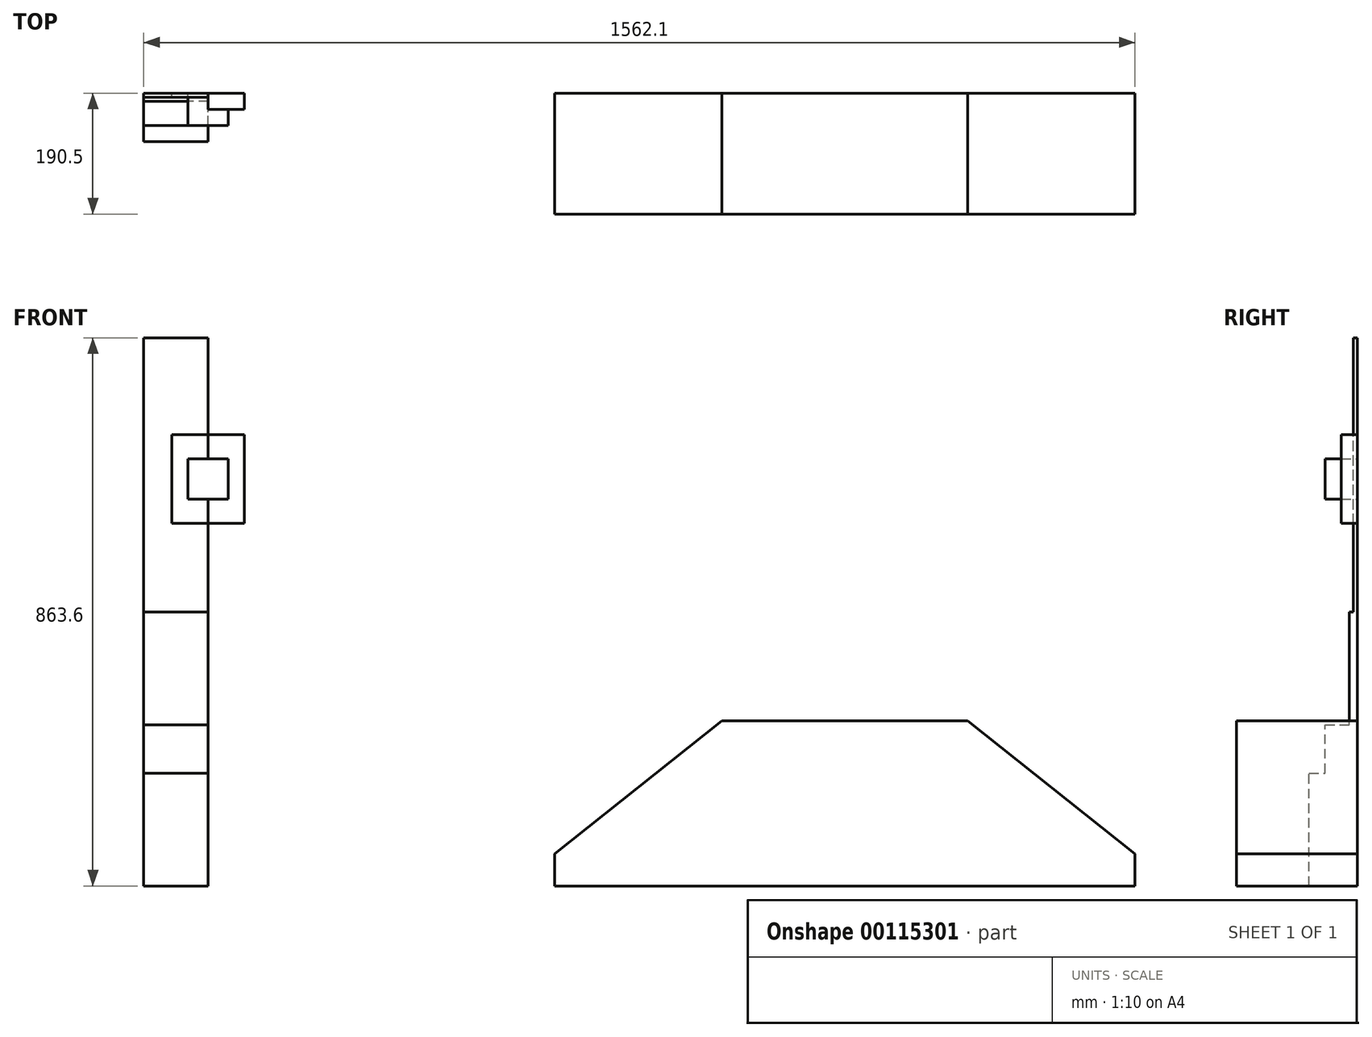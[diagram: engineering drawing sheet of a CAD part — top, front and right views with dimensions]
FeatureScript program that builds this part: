
annotation { "Feature Type Name" : "Feature", "Feature Type Description" : "" }
export const myFeature = defineFeature(function(context is Context, id is Id, definition is map)
    precondition{}
    {
        {
            var Q0;
            Q0=qCreatedBy(makeId("Front.planeOp"),FACE);
            var sketch = newSketch(context, id + "F0", { "sketchPlane" : qUnion([Q0])});
            skLineSegment(sketch, "E0", {"start": v(0, 0) * mm, "end": v(914.4, 0) * mm});
            skLineSegment(sketch, "E1", {"start": v(914.4, 0) * mm, "end": v(914.4, 50.8) * mm});
            skLineSegment(sketch, "E2", {"start": v(914.4, 50.8) * mm, "end": v(650.88, 260.35) * mm});
            skLineSegment(sketch, "E3", {"start": v(650.88, 260.35) * mm, "end": v(263.53, 260.35) * mm});
            skLineSegment(sketch, "E4", {"start": v(263.53, 260.35) * mm, "end": v(0, 50.8) * mm});
            skLineSegment(sketch, "E5", {"start": v(0, 50.8) * mm, "end": v(0, 0) * mm});
            skLineSegment(sketch, "E6.bottom", {"start": v(-546.1, 0) * mm, "end": v(-647.7, 0) * mm});
            skLineSegment(sketch, "E6.top", {"start": v(-546.1, 177.8) * mm, "end": v(-647.7, 177.8) * mm});
            skLineSegment(sketch, "E6.left", {"start": v(-546.1, 0) * mm, "end": v(-546.1, 177.8) * mm});
            skLineSegment(sketch, "E6.right", {"start": v(-647.7, 0) * mm, "end": v(-647.7, 177.8) * mm});
            skLineSegment(sketch, "E7.top", {"start": v(-546.1, 254) * mm, "end": v(-647.7, 254) * mm});
            skLineSegment(sketch, "E7.left", {"start": v(-546.1, 177.8) * mm, "end": v(-546.1, 254) * mm});
            skLineSegment(sketch, "E7.right", {"start": v(-647.7, 177.8) * mm, "end": v(-647.7, 254) * mm});
            skLineSegment(sketch, "E8.top", {"start": v(-546.1, 431.8) * mm, "end": v(-647.7, 431.8) * mm});
            skLineSegment(sketch, "E8.left", {"start": v(-546.1, 254) * mm, "end": v(-546.1, 431.8) * mm});
            skLineSegment(sketch, "E8.right", {"start": v(-647.7, 254) * mm, "end": v(-647.7, 431.8) * mm});
            skLineSegment(sketch, "E9.top", {"start": v(-546.1, 863.6) * mm, "end": v(-647.7, 863.6) * mm});
            skLineSegment(sketch, "E9.left", {"start": v(-546.1, 431.8) * mm, "end": v(-546.1, 863.6) * mm});
            skLineSegment(sketch, "E9.right", {"start": v(-647.7, 431.8) * mm, "end": v(-647.7, 863.6) * mm});
            skLineSegment(sketch, "E10.bottom", {"start": v(-488.95, 571.5) * mm, "end": v(-546.1, 571.5) * mm});
            skLineSegment(sketch, "E10.top", {"start": v(-488.95, 711.2) * mm, "end": v(-603.25, 711.2) * mm});
            skLineSegment(sketch, "E10.left", {"start": v(-488.95, 571.5) * mm, "end": v(-488.95, 711.2) * mm});
            skLineSegment(sketch, "E10.right", {"start": v(-603.25, 571.5) * mm, "end": v(-603.25, 711.2) * mm});
            skPoint(sketch, "E10.middle", {"position": v(-546.1, 641.35) * mm});
            skLineSegment(sketch, "E11.bottom", {"start": v(-514.35, 609.6) * mm, "end": v(-577.85, 609.6) * mm});
            skLineSegment(sketch, "E11.top", {"start": v(-514.35, 673.1) * mm, "end": v(-577.85, 673.1) * mm});
            skLineSegment(sketch, "E11.left", {"start": v(-514.35, 609.6) * mm, "end": v(-514.35, 673.1) * mm});
            skLineSegment(sketch, "E11.right", {"start": v(-577.85, 609.6) * mm, "end": v(-577.85, 673.1) * mm});
            skLineSegment(sketch, "E12", {"start": v(-546.1, 571.5) * mm, "end": v(-603.25, 571.5) * mm});
            skLineSegment(sketch, "E13", {"start": v(-546.1, 431.8) * mm, "end": v(-546.1, 571.5) * mm, "construction": true});
            skLineSegment(sketch, "E14", {"start": v(914.4, 0) * mm, "end": v(1244.6, 0) * mm, "construction": true});
            skLineSegment(sketch, "E15", {"start": v(1244.6, 0) * mm, "end": v(1244.6, 1297.5) * mm, "construction": true});
            skLineSegment(sketch, "E16", {"start": v(-1249.64, 584.2) * mm, "end": v(1517.37, 584.2) * mm, "construction": true});
            skLineSegment(sketch, "E17", {"start": v(-1249.64, 508) * mm, "end": v(1517.37, 508) * mm, "construction": true});
            skLineSegment(sketch, "E18", {"start": v(-685.8, 0) * mm, "end": v(-685.8, 1284.2) * mm, "construction": true});
            skLineSegment(sketch, "E19", {"start": v(-647.7, 0) * mm, "end": v(-962.03, 0) * mm, "construction": true});
            skLineSegment(sketch, "E20", {"start": v(-962.03, 0) * mm, "end": v(-962.03, -101.6) * mm, "construction": true});
            skLineSegment(sketch, "E21", {"start": v(-962.03, -101.6) * mm, "end": v(-1876.43, -101.6) * mm, "construction": true});
            skLineSegment(sketch, "E22", {"start": v(-1876.43, -101.6) * mm, "end": v(-1876.43, 0) * mm, "construction": true});
            skLineSegment(sketch, "E23", {"start": v(-1981.2, 0) * mm, "end": v(-1981.2, 1220.8) * mm, "construction": true});
            skLineSegment(sketch, "E24", {"start": v(-1876.43, 0) * mm, "end": v(-1981.2, 0) * mm, "construction": true});
            skSolve(sketch);
        }
        {
            var Q0;
            Q0=makeQuery(id+"F0.imprint","IMPRINT",FACE,{"disambiguationData":[TD([[makeQuery(id+"F0.imprint","IMPRINT",EDGE,{"derivedFrom":sQuery(id+"F0.wireOp",EDGE,"E0")}),1.0]])]});
            extrude(context, id + "F1", {"entities" : qUnion([Q0]), "depth" : 190.5 * mm});
        }
        {
            var Q0;
            Q0=makeQuery(id+"F0.imprint","IMPRINT",FACE,{"disambiguationData":[TD([[makeQuery(id+"F0.imprint","IMPRINT",EDGE,{"derivedFrom":sQuery(id+"F0.wireOp",EDGE,"E6.bottom")}),-1.0]])]});
            extrude(context, id + "F2", {"entities" : qUnion([Q0]), "depth" : 76.2 * mm});
        }
        {
            var Q0;
            Q0=makeQuery(id+"F0.imprint","IMPRINT",FACE,{"disambiguationData":[TD([[makeQuery(id+"F0.imprint","IMPRINT",EDGE,{"derivedFrom":sQuery(id+"F0.wireOp",EDGE,"E6.top")}),-1.0]])]});
            extrude(context, id + "F3", {"entities" : qUnion([Q0]), "operationType" : NewBodyOperationType.ADD, "depth" : 50.8 * mm});
        }
        {
            var Q0;
            Q0=makeQuery(id+"F0.imprint","IMPRINT",FACE,{"disambiguationData":[TD([[makeQuery(id+"F0.imprint","IMPRINT",EDGE,{"derivedFrom":sQuery(id+"F0.wireOp",EDGE,"E7.top")}),-1.0]])]});
            extrude(context, id + "F4", {"entities" : qUnion([Q0]), "operationType" : NewBodyOperationType.ADD, "depth" : 12.7 * mm});
        }
        {
            var Q0;
            Q0=makeQuery(id+"F0.imprint","IMPRINT",FACE,{"disambiguationData":[TD([[makeQuery(id+"F0.imprint","IMPRINT",EDGE,{"derivedFrom":sQuery(id+"F0.wireOp",EDGE,"E9.top")}),1.0]])]});
            extrude(context, id + "F5", {"entities" : qUnion([Q0]), "operationType" : NewBodyOperationType.ADD, "depth" : 6.35 * mm});
        }
        {
            var Q0;
            Q0=makeQuery(id+"F0.imprint","IMPRINT",FACE,{"disambiguationData":[TD([[makeQuery(id+"F0.imprint","IMPRINT",EDGE,{"derivedFrom":sQuery(id+"F0.wireOp",EDGE,"E11.bottom")}),-1.0]])]});
            extrude(context, id + "F6", {"entities" : qUnion([Q0]), "depth" : 50.8 * mm});
        }
        {
            var Q0;
            Q0=makeQuery(id+"F0.imprint","IMPRINT",FACE,{"disambiguationData":[TD([[makeQuery(id+"F0.imprint","IMPRINT",EDGE,{"derivedFrom":sQuery(id+"F0.wireOp",EDGE,"E10.bottom")}),-1.0]])]});
            extrude(context, id + "F7", {"entities" : qUnion([Q0]), "operationType" : NewBodyOperationType.ADD, "depth" : 25.4 * mm});
        }
    });
